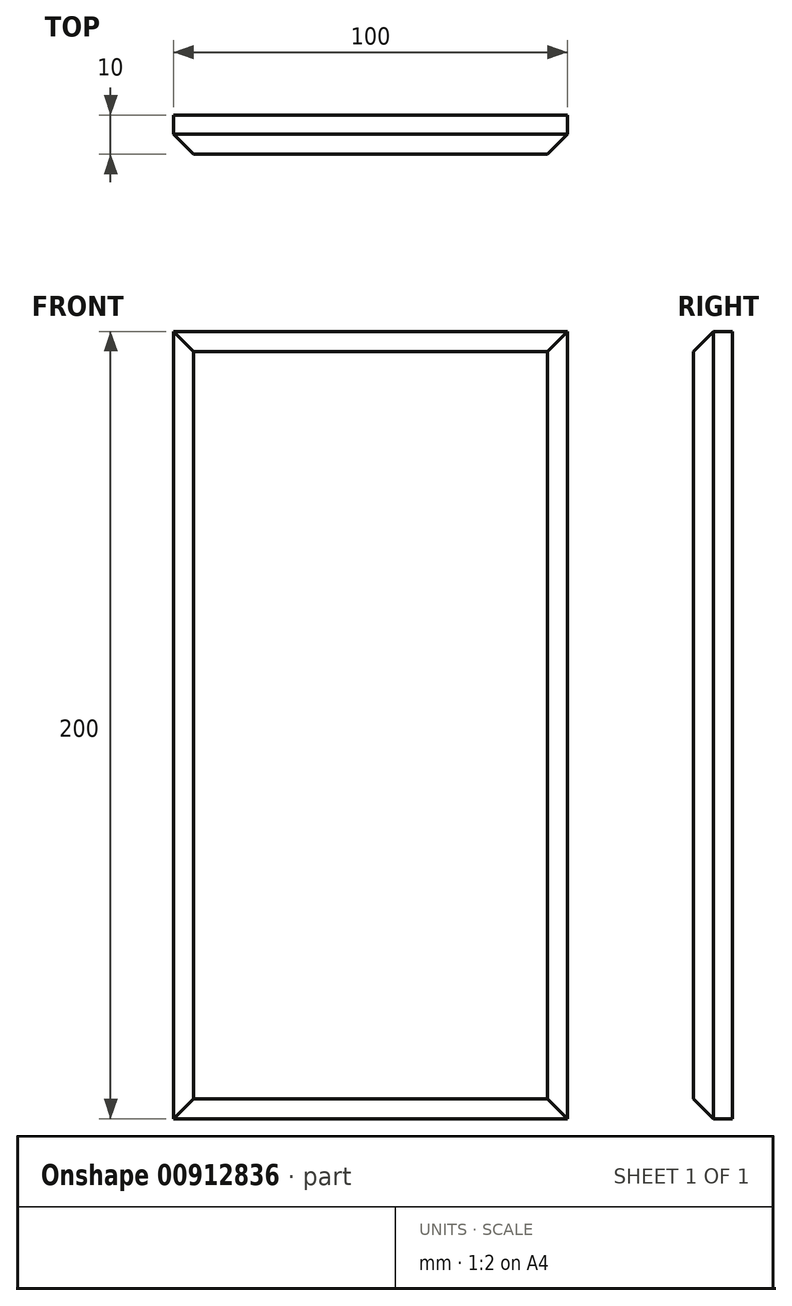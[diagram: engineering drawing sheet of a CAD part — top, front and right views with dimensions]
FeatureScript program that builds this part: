
annotation { "Feature Type Name" : "Feature", "Feature Type Description" : "" }
export const myFeature = defineFeature(function(context is Context, id is Id, definition is map)
    precondition{}
    {
        {
            var Q0;
            Q0=qCreatedBy(makeId("Front.planeOp"),FACE);
            var sketch = newSketch(context, id + "F0", { "sketchPlane" : qUnion([Q0])});
            skLineSegment(sketch, "E0.bottom", {"start": v(-50, 100) * mm, "end": v(50, 100) * mm});
            skLineSegment(sketch, "E0.top", {"start": v(-50, -100) * mm, "end": v(50, -100) * mm});
            skLineSegment(sketch, "E0.left", {"start": v(-50, 100) * mm, "end": v(-50, -100) * mm});
            skLineSegment(sketch, "E0.right", {"start": v(50, 100) * mm, "end": v(50, -100) * mm});
            skPoint(sketch, "E0.middle", {"position": v(0, 0) * mm});
            skSolve(sketch);
        }
        {
            var Q0;
            Q0 = qSketchRegion(id + "F0", true);
            extrude(context, id + "F1", {"entities" : qUnion([Q0]), "depth" : 10 * mm, "offsetDistance" : 25.4 * mm});
        }
        {
            var Q0;
            Q0=makeQuery(id+"F1.opExtrude","CAP_EDGE",EDGE,{"disambiguationData":[OSD([sQuery(id+"F0.wireOp",EDGE,"E0.left")])],"isStart":false});
            var Q1;
            Q1=makeQuery(id+"F1.opExtrude","CAP_EDGE",EDGE,{"disambiguationData":[OSD([sQuery(id+"F0.wireOp",EDGE,"E0.bottom")])],"isStart":false});
            var Q2;
            Q2=makeQuery(id+"F1.opExtrude","CAP_EDGE",EDGE,{"disambiguationData":[OSD([sQuery(id+"F0.wireOp",EDGE,"E0.top")])],"isStart":false});
            var Q3;
            Q3=makeQuery(id+"F1.opExtrude","CAP_EDGE",EDGE,{"disambiguationData":[OSD([sQuery(id+"F0.wireOp",EDGE,"E0.right")])],"isStart":false});
            chamfer(context, id + "F2", {"entities" : qUnion([Q0, Q1, Q2, Q3]), "width" : 5.08 * mm, "tangentPropagation" : true});
        }
        {
            var Q0;
            Q0=makeQuery(id+"F1.opExtrude","CAP_FACE",FACE,{"disambiguationData":[OSD([sQuery(id+"F0.wireOp",EDGE,"E0.bottom"),sQuery(id+"F0.wireOp",EDGE,"E0.top"),sQuery(id+"F0.wireOp",EDGE,"E0.left"),sQuery(id+"F0.wireOp",EDGE,"E0.right")])],"isStart":true});
            var sketch = newSketch(context, id + "F3", { "sketchPlane" : qUnion([Q0])});
            skCircle(sketch, "E1", {"center": v(0, 0) * mm, "radius": 46.54 * mm});
            skSolve(sketch);
        }
        {
            var Q0;
            Q0=sQuery(id+"F3.wireOp",EDGE,"E1");
            extrude(context, id + "F4", {"bodyType" : ToolBodyType.SURFACE, "surfaceEntities" : qUnion([Q0]), "depth" : -3 * mm, "offsetDistance" : 25.4 * mm});
        }
    });
